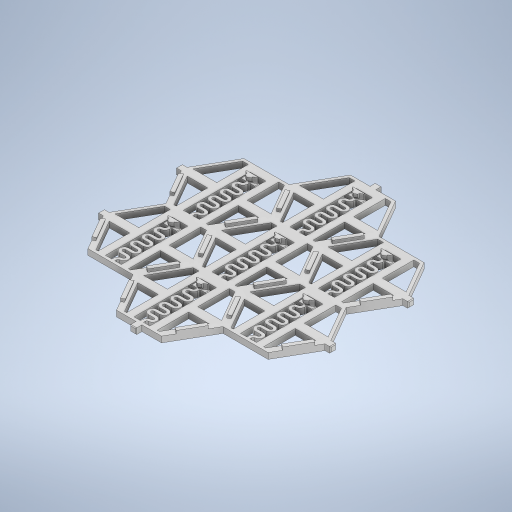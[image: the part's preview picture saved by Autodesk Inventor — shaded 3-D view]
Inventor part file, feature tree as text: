
AUTODESK INVENTOR PART (.ipt)
format: ipt  version: 2024 (Build 280153000, 153)  size: 1,856,512 bytes
history: native  units: in
note: dims shown in document units (in); Inventor stores cm internally (conversion verified against a paired STEP export)
features: move_body x29, direct_edit x19, extrude x12, sketch x6, chamfer x5, draft x2, plane x2, pattern_linear x1, pattern_circular x1, boolean_combine x1, other x1
ambient origin geometry x8: Origin, YZ Plane, XZ Plane, XY Plane, X Axis, Y Axis, Z Axis, Center Point
bodies: Solid1 (feature_tree), Solid8 (feature_tree)
feature tree (79):
  sketch  "Sketch1"  dims[d0=0.5217in d1=1.939in d2=120.0deg d3=120.0deg d4=0.4134in d5=0.9695in d6=0.0709in d7=0.0709in d8=0.1378in d9=0.8268in d10=0.1181in]
  extrude  "Extrusion1"  Depth=0.1181in
  extrude  "Extrusion2"  Depth=0.0787in
  extrude  "Extrusion3"  Depth=0.0787in
  chamfer  "Chamfer1"  Distance=0.315in
  extrude  "Extrusion4"  Depth=0.0394in
  chamfer  "Chamfer2"  Distance=0.0787in
  direct_edit  "Direct Edit1"
  direct_edit  "Direct Edit2"
  direct_edit  "Direct Edit3"
  direct_edit  "Direct Edit4"
  direct_edit  "Direct Edit5"
  direct_edit  "Direct Edit6"
  direct_edit  "Direct Edit7"
  direct_edit  "Direct Edit8"
  direct_edit  "Direct Edit9"
  direct_edit  "Direct Edit10"
  extrude  "Extrusion7"  Depth=0.315in
  chamfer  "Chamfer3"  Distance=0.0157in
  direct_edit  "Direct Edit11"
  direct_edit  "Direct Edit12"
  extrude  "Extrusion8"  Depth=0.0787in
  extrude  "Extrusion9"  Depth=0.1181in
  draft  "FaceDraft1"
  draft  "FaceDraft2"
  direct_edit  "Direct Edit13"
  direct_edit  "Direct Edit14"
  direct_edit  "Direct Edit15"
  direct_edit  "Direct Edit16"
  direct_edit  "Direct Edit17"
  direct_edit  "Direct Edit18"
  direct_edit  "Direct Edit19"
  extrude  "Extrusion10"  Depth=0.1969in
  chamfer  "Chamfer4"  Distance=0.0787in
  pattern_linear  "Rectangular Pattern1"  Spacing1=0.1181in  [1 undecoded]
  pattern_circular  "Circular Pattern2"  [2 undecoded]
  boolean_combine  "Combine1"
  plane  "Work Plane1"
  extrude  "Extrusion11"  Depth=0.0787in
  plane  "Work Plane2"
  extrude  "Extrusion12"  Depth=0.0787in
  sketch  "Sketch7"  dims[d17=0.0394in d19=1.5748in d21=0.315in d22=0.3937in d24=0.3937in d26=0.0394in d27=0.0787in d28=0.315in d29=0.0157in d30=0.0157in d31=0.1181in d32=0.1969in d33=0.0787in d34=0.0in d35=0.1181in d36=0.0in d37=0.0787in d38=0.0079in d39=0.0787in d40=0.0079in d41=0.0787in d42=0.0079in d43=0.0079in d44=0.0787in d45=0.0394in d46=0.0197in d47=0.0394in d48=0.0in d49=0.0197in d50=0.0787in d51=45.0deg d52=0.0197in d53=0.0in d54=0.0079in d55=0.0787in d56=45.0deg d57=0.0in d58=0.0in d59=0.0098in d60=0.0in d61=0.0in d62=0.0098in d63=0.0in d64=0.0in d65=-0.0197in d66=0.0in d67=0.0in d68=-0.0197in d69=0.0in d70=0.0in d71=0.0153in d72=0.0in d73=0.0in d74=0.0153in d75=0.0in d76=0.0in d77=0.0153in d78=0.0in d79=0.0in d80=0.0153in d81=0.0in d82=0.0in d83=0.0394in d84=0.0in d85=0.0in d86=0.0394in d87=0.0in d88=0.0in d89=-0.0278in d90=0.0in d91=0.0in d92=-0.0278in d93=0.0in d94=0.0in d95=-0.0278in d96=0.0in d97=0.0in d98=-0.0278in d99=0.0in d100=-0.0157in d101=0.0in d102=0.0in d103=0.0157in d104=0.0in d116=0.0in d117=0.0in d118=0.0394in d119=0.1181in d120=0.0in d121=0.0276in d122=0.0787in d123=45.0deg d124=-0.0625in d125=0.0in d126=0.0in d127=0.0079in d128=0.0in d129=0.0in d130=0.315in d131=0.6299in d132=0.0787in d133=0.1575in d134=0.0in d135=0.1575in d136=0.0in d137=-0.1031in d138=-0.1031in d139=0.0591in d140=0.0in d141=0.0in d142=0.0in d143=-0.0197in d144=0.0in d145=0.0in d146=0.0197in d147=0.0in d148=0.0in d149=0.0in d150=0.0079in d151=0.0in d152=0.0in d153=0.0079in d154=0.0in d155=0.0in d156=0.0079in d157=0.0in d158=0.0in d159=0.0079in d163=0.0in d164=0.0in d165=-0.2992in d166=0.0in d167=0.0in d168=0.0039in d169=0.0in d170=0.0in d171=-0.0295in d172=1.378in d173=0.122in d174=0.122in d175=0.122in d176=0.122in d177=0.122in d178=0.0in d179=0.0197in d180=0.0787in d181=45.0deg d245=0.7874in d247=2.0965in d248=2.3622in d249=360.0deg d251=0.0787in d252=0.0787in d253=0.1969in d254=0.0in d255=-6.0525in d256=0.1969in d257=0.0in d258=0.0787in d259=0.0787in d260=0.1575in d261=0.0in d262=0.1575in d263=0.0in d264=0.0197in d265=0.0787in d266=45.0deg]
  extrude  "Extrusion13"  Depth=0.0787in
  extrude  "Extrusion14"  Depth=0.0787in
  chamfer  "Chamfer5"  Distance=0.0079in
  sketch  "Sketch3"  dims[d11=0.0394in d12=0.0787in]
  sketch  "Sketch4"  dims[d13=0.0394in d14=0.0787in]
  other  "Pattern of Solid1:7"
  sketch  "Sketch5"  dims[d15=0.0591in]
  sketch  "Sketch6"  dims[d16=0.0394in]
  move_body  "Move1"
  move_body  "Move2"
  move_body  "Move3"
  move_body  "Move4"
  move_body  "Move5"
  move_body  "Move6"
  move_body  "Move7"
  move_body  "Move8"
  move_body  "Move9"
  move_body  "Move10"
  move_body  "Move11"
  move_body  "Move12"
  move_body  "Move13"
  move_body  "Move14"
  move_body  "Move15"
  move_body  "Move16"
  move_body  "Move18"
  move_body  "Move19"
  move_body  "Move20"
  move_body  "Move21"
  move_body  "Move22"
  move_body  "Move23"
  move_body  "Move24"
  move_body  "Move25"
  move_body  "Move26"
  move_body  "Move27"
  move_body  "Move29"
  move_body  "Move30"
  move_body  "Move31"
note: 3 required parameter values undecoded (feature->parameter linkage not recoverable at this tier; creation-order binding heuristic only, values carry confidence <= 0.55)
